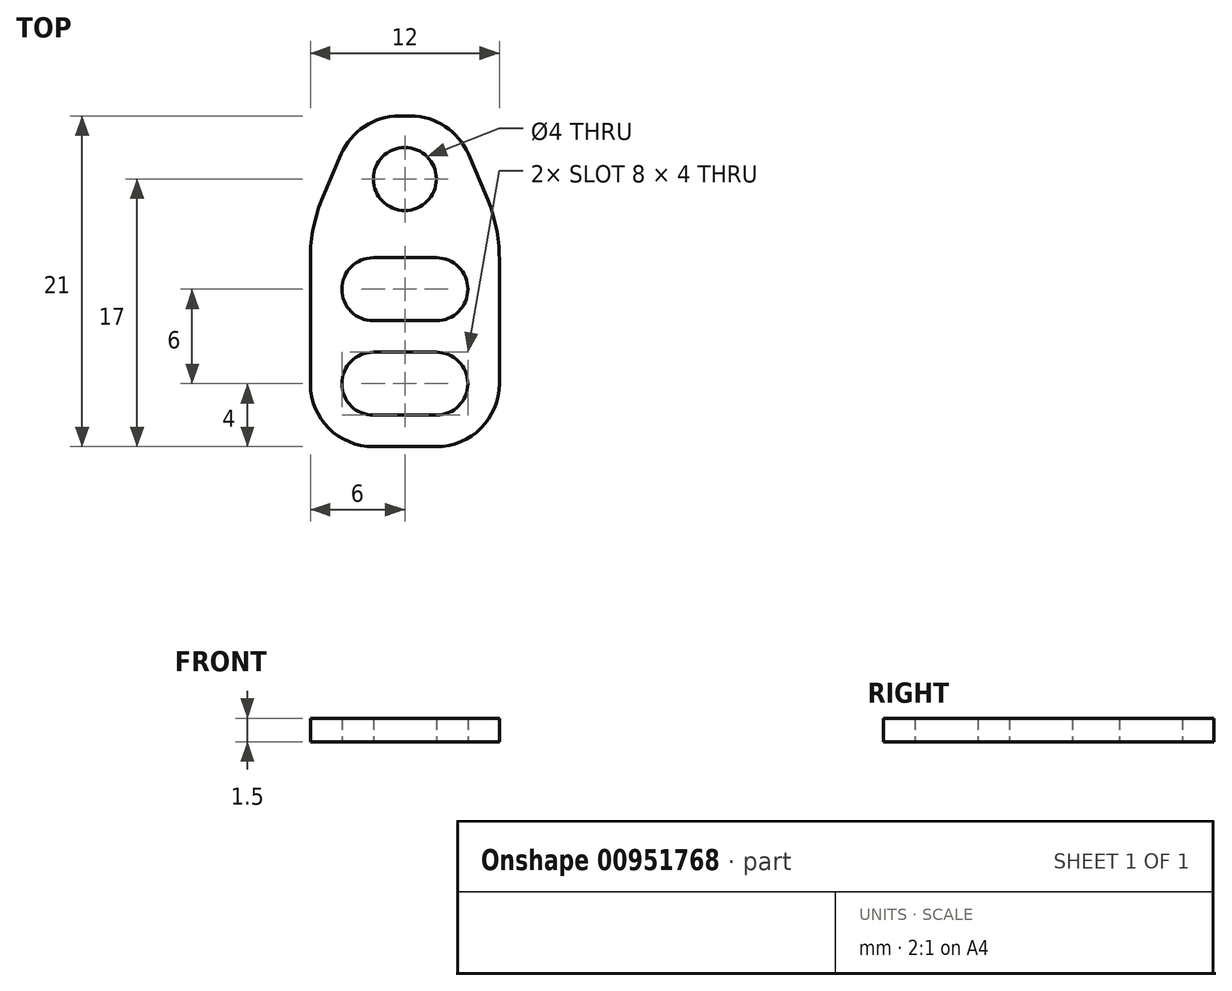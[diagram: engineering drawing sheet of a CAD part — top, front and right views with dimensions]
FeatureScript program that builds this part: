
annotation { "Feature Type Name" : "Feature", "Feature Type Description" : "" }
export const myFeature = defineFeature(function(context is Context, id is Id, definition is map)
    precondition{}
    {
        {
            var Q0;
            Q0=qCreatedBy(makeId("Top.planeOp"),FACE);
            var sketch = newSketch(context, id + "F0", { "sketchPlane" : qUnion([Q0])});
            skLineSegment(sketch, "E0.bottom", {"start": v(3, 10.5) * mm, "end": v(-3, 10.5) * mm});
            skLineSegment(sketch, "E0.top", {"start": v(6, -10.5) * mm, "end": v(-6, -10.5) * mm});
            skLineSegment(sketch, "E0.left", {"start": v(6, 3.5) * mm, "end": v(6, -10.5) * mm});
            skLineSegment(sketch, "E0.right", {"start": v(-6, 3.5) * mm, "end": v(-6, -10.5) * mm});
            skPoint(sketch, "E0.middle", {"position": v(0, 0) * mm});
            skCircle(sketch, "E1", {"center": v(-2, -6.5) * mm, "radius": 2 * mm});
            skCircle(sketch, "E2", {"center": v(2, -6.5) * mm, "radius": 2 * mm});
            skCircle(sketch, "E3", {"center": v(-2, -0.5) * mm, "radius": 2 * mm});
            skCircle(sketch, "E4", {"center": v(2, -0.5) * mm, "radius": 2 * mm});
            skCircle(sketch, "E5", {"center": v(0, 6.5) * mm, "radius": 2 * mm});
            skLineSegment(sketch, "E6.bottom", {"start": v(2, -2.5) * mm, "end": v(-2, -2.5) * mm});
            skLineSegment(sketch, "E6.top", {"start": v(2, 1.5) * mm, "end": v(-2, 1.5) * mm});
            skLineSegment(sketch, "E6.left", {"start": v(2, -2.5) * mm, "end": v(2, 1.5) * mm});
            skLineSegment(sketch, "E7.bottom", {"start": v(2, -8.5) * mm, "end": v(-2, -8.5) * mm});
            skLineSegment(sketch, "E7.top", {"start": v(2, -4.5) * mm, "end": v(-2, -4.5) * mm});
            skLineSegment(sketch, "E7.left", {"start": v(2, -8.5) * mm, "end": v(2, -4.5) * mm});
            skLineSegment(sketch, "E7.right", {"start": v(-2, -8.5) * mm, "end": v(-2, -4.5) * mm});
            skLineSegment(sketch, "E8", {"start": v(3, 10.5) * mm, "end": v(6, 3.5) * mm});
            skLineSegment(sketch, "E9.MirrorCS", {"start": v(-3, 10.5) * mm, "end": v(-6, 3.5) * mm});
            skPoint(sketch, "E10.orphan", {"position": v(-6, 10.5) * mm});
            skPoint(sketch, "E11.orphan", {"position": v(6, 10.5) * mm});
            skLineSegment(sketch, "E12.trimOffspring", {"start": v(-0.02, -0.79) * mm, "end": v(0.02, -0.79) * mm});
            skLineSegment(sketch, "E13.trimOffspring", {"start": v(-0.02, -0.21) * mm, "end": v(0.02, -0.21) * mm});
            skSolve(sketch);
        }
        {
            var Q0;
            Q0=makeQuery(id+"F0.imprint","IMPRINT",FACE,{"disambiguationData":[TD([[makeQuery(id+"F0.imprint","IMPRINT",EDGE,{"derivedFrom":sQuery(id+"F0.wireOp",EDGE,"E0.bottom")}),1.0]])]});
            extrude(context, id + "F1", {"entities" : qUnion([Q0]), "depth" : 1.5 * mm, "offsetDistance" : 25 * mm});
        }
        {
            var Q0;
            Q0=makeQuery(id+"F1.opExtrude","SWEPT_EDGE",EDGE,{"disambiguationData":[OSD([sQuery(id+"F0.wireOp",EDGE,"E0.bottom"),sQuery(id+"F0.wireOp",EDGE,"E8")])]});
            var Q1;
            Q1=makeQuery(id+"F1.opExtrude","SWEPT_EDGE",EDGE,{"disambiguationData":[OSD([sQuery(id+"F0.wireOp",EDGE,"E0.bottom"),sQuery(id+"F0.wireOp",EDGE,"E9.MirrorCS")])]});
            fillet(context, id + "F2", {"entities" : qUnion([Q0, Q1]), "radius" : 4 * mm, "tangentPropagation" : true, "allowEdgeOverflow" : false});
        }
        {
            var Q0;
            Q0=makeQuery(id+"F1.opExtrude","SWEPT_EDGE",EDGE,{"disambiguationData":[OSD([sQuery(id+"F0.wireOp",EDGE,"E0.right"),sQuery(id+"F0.wireOp",EDGE,"E9.MirrorCS")])]});
            var Q1;
            Q1=makeQuery(id+"F1.opExtrude","SWEPT_EDGE",EDGE,{"disambiguationData":[OSD([sQuery(id+"F0.wireOp",EDGE,"E0.left"),sQuery(id+"F0.wireOp",EDGE,"E8")])]});
            fillet(context, id + "F3", {"entities" : qUnion([Q0, Q1]), "radius" : 10 * mm, "tangentPropagation" : true, "allowEdgeOverflow" : false});
        }
        {
            var Q0;
            Q0=makeQuery(id+"F1.opExtrude","SWEPT_EDGE",EDGE,{"disambiguationData":[OSD([sQuery(id+"F0.wireOp",EDGE,"E0.top"),sQuery(id+"F0.wireOp",EDGE,"E0.right")])]});
            var Q1;
            Q1=makeQuery(id+"F1.opExtrude","SWEPT_EDGE",EDGE,{"disambiguationData":[OSD([sQuery(id+"F0.wireOp",EDGE,"E0.top"),sQuery(id+"F0.wireOp",EDGE,"E0.left")])]});
            fillet(context, id + "F4", {"entities" : qUnion([Q0, Q1]), "radius" : 4 * mm, "tangentPropagation" : true, "allowEdgeOverflow" : false});
        }
    });
